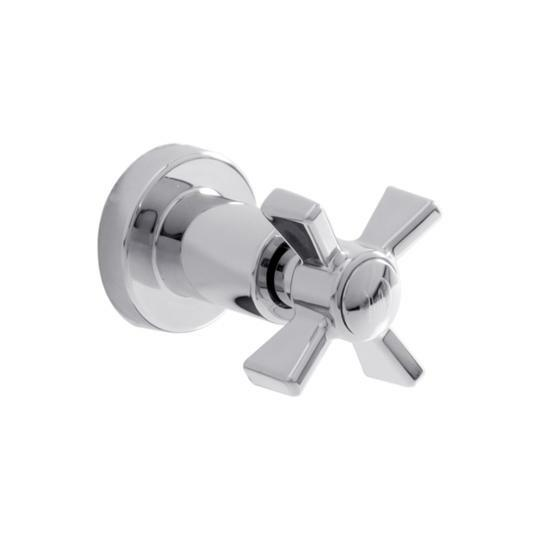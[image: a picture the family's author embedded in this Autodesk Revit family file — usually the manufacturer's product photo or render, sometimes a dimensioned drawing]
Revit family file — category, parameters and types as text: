
# Revit family: 01-1633-11 REGISTRO DUCHA HELIX CRUZ
name_source: partatom
category: Aparatos sanitarios
revit_build: Autodesk Revit 2018 (Build: 20170223_1515(x64)
units: mm (PartAtom-declared; Revit-internal decimal feet)

## family parameters
Anfitrión = Cara
Compartido = No
Corte con vacíos al cargar = No
Cota de conector redondo = Diámetro de uso
Número OmniClass = 23.31.11.00
Punto de cálculo de habitación = No
Tipo de pieza = Normal

## types (1)
- 01-1633-11
    Alto = 56 mm
    Ancho = 60 mm
    Conexión AC = Sí
    Conexión AF = Sí
    Conexión de residuos = No
    Conexión de ventilación = No
    Descripción = Registro ducha
    Elevación por defecto = 0 mm  [stored 0 ft]
    Fabricante = Gricol
    Imagen de tipo = <Ninguno>
    Link Ficha Tecnica = http://infotecnica.gricol.com
    Modelo = 01-1633-11
    Plastico ABS Cromado = Plastico ABS Cromado
    Product Name = 01-1633-11 REGISTRO DUCHA HELIX CRUZ
    Profundidad = 85 mm
    URL = https://www.gricol.com

note: [stored X ft] marks values corroborated as IEEE doubles in the binary element streams (Revit-internal decimal feet)

## geometry (parser evidence)
native form markers: Blend x2, Sweep x2
no freeform markers — native parametric forms only
